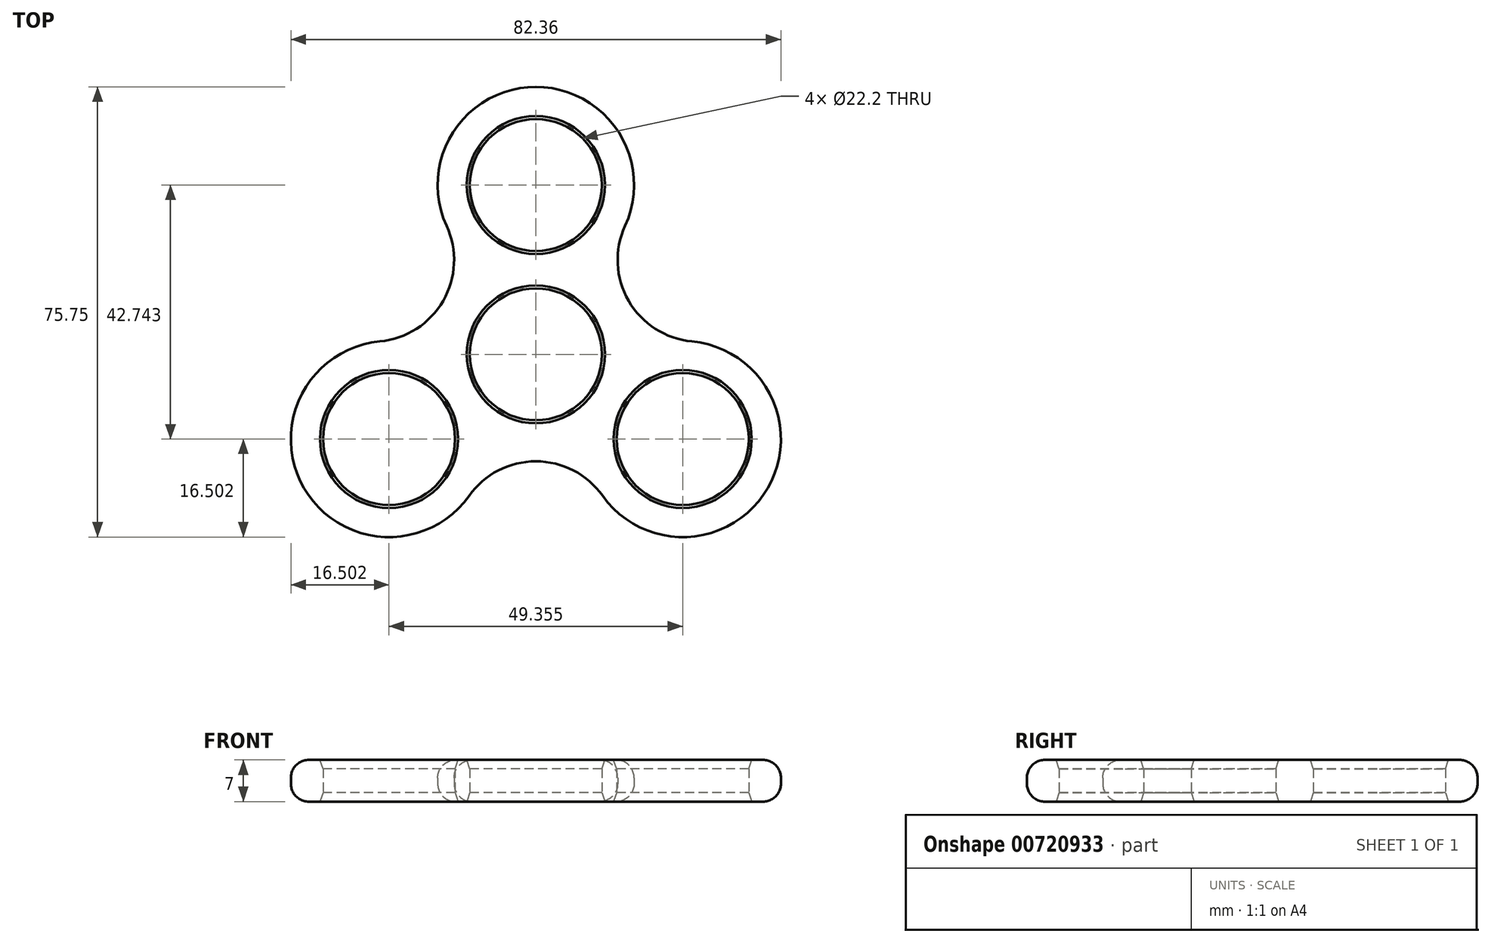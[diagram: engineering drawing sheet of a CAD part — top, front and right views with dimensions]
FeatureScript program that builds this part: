
annotation { "Feature Type Name" : "Feature", "Feature Type Description" : "" }
export const myFeature = defineFeature(function(context is Context, id is Id, definition is map)
    precondition{}
    {
        {
            var Q0;
            Q0=qCreatedBy(makeId("Top.planeOp"),FACE);
            var sketch = newSketch(context, id + "F0", { "sketchPlane" : qUnion([Q0])});
            skLineSegment(sketch, "E0", {"start": v(0, 0) * mm, "end": v(-15.59, 9) * mm, "construction": true});
            skArc(sketch, "E1", {"start": v(0, 45) * mm, "mid": v(-13.9, 37.4) * mm, "end": v(-15, 21.6) * mm});
            skArc(sketch, "E2", {"start": v(-15, 21.6) * mm, "mid": v(-13.76, 15.23) * mm, "end": v(-15.59, 9) * mm});
            skLineSegment(sketch, "E3", {"start": v(0, 0) * mm, "end": v(0, 45) * mm, "construction": true});
            skArc(sketch, "E4.MirrorCS", {"start": v(15, 21.6) * mm, "mid": v(13.76, 15.23) * mm, "end": v(15.59, 9) * mm});
            skArc(sketch, "E5.MirrorCS", {"start": v(0, 45) * mm, "mid": v(13.9, 37.4) * mm, "end": v(15, 21.6) * mm});
            skArc(sketch, "E6.1.0", {"start": v(-11.21, -23.8) * mm, "mid": v(-6.31, -19.53) * mm, "end": v(0, -18) * mm});
            skArc(sketch, "E6.1.1", {"start": v(-38.97, -22.5) * mm, "mid": v(-25.45, -30.73) * mm, "end": v(-11.21, -23.8) * mm});
            skArc(sketch, "E6.1.2", {"start": v(-38.97, -22.5) * mm, "mid": v(-39.34, -6.67) * mm, "end": v(-26.21, 2.19) * mm});
            skArc(sketch, "E6.1.3", {"start": v(-26.21, 2.19) * mm, "mid": v(-20.07, 4.3) * mm, "end": v(-15.59, 9) * mm});
            skArc(sketch, "E6.2.0", {"start": v(26.21, 2.19) * mm, "mid": v(20.07, 4.3) * mm, "end": v(15.59, 9) * mm});
            skArc(sketch, "E6.2.1", {"start": v(38.97, -22.5) * mm, "mid": v(39.34, -6.67) * mm, "end": v(26.21, 2.19) * mm});
            skArc(sketch, "E6.2.2", {"start": v(38.97, -22.5) * mm, "mid": v(25.45, -30.73) * mm, "end": v(11.21, -23.8) * mm});
            skArc(sketch, "E6.2.3", {"start": v(11.21, -23.8) * mm, "mid": v(6.31, -19.53) * mm, "end": v(0, -18) * mm});
            skPoint(sketch, "E6.center", {"position": v(0, 0) * mm});
            skCircle(sketch, "E7", {"center": v(0, 0) * mm, "radius": 11.1 * mm});
            skCircle(sketch, "E8", {"center": v(0, 28.5) * mm, "radius": 11.1 * mm});
            skCircle(sketch, "E9.1.1", {"center": v(-24.68, -14.25) * mm, "radius": 11.1 * mm});
            skCircle(sketch, "E9.2.1", {"center": v(24.68, -14.25) * mm, "radius": 11.1 * mm});
            skSolve(sketch);
        }
        {
            var Q0;
            Q0=makeQuery(id+"F0.imprint","IMPRINT",FACE,{"disambiguationData":[TD([[makeQuery(id+"F0.imprint","IMPRINT",EDGE,{"derivedFrom":sQuery(id+"F0.wireOp",EDGE,"E1")}),1.0]])]});
            extrude(context, id + "F1", {"entities" : qUnion([Q0]), "depth" : 7 * mm});
        }
        {
            var Q0;
            Q0=makeQuery(id+"F1.opExtrude","CAP_EDGE",EDGE,{"disambiguationData":[OSD([sQuery(id+"F0.wireOp",EDGE,"E6.1.1"),sQuery(id+"F0.wireOp",EDGE,"E6.1.2")])],"isStart":false});
            var Q1;
            Q1=makeQuery(id+"F1.opExtrude","CAP_EDGE",EDGE,{"disambiguationData":[OSD([sQuery(id+"F0.wireOp",EDGE,"E6.1.0"),sQuery(id+"F0.wireOp",EDGE,"E6.2.3")])],"isStart":false});
            var Q2;
            Q2=makeQuery(id+"F1.opExtrude","CAP_EDGE",EDGE,{"disambiguationData":[OSD([sQuery(id+"F0.wireOp",EDGE,"E6.2.1"),sQuery(id+"F0.wireOp",EDGE,"E6.2.2")])],"isStart":false});
            var Q3;
            Q3=makeQuery(id+"F1.opExtrude","CAP_EDGE",EDGE,{"disambiguationData":[OSD([sQuery(id+"F0.wireOp",EDGE,"E4.MirrorCS"),sQuery(id+"F0.wireOp",EDGE,"E6.2.0")])],"isStart":false});
            var Q4;
            Q4=makeQuery(id+"F1.opExtrude","CAP_EDGE",EDGE,{"disambiguationData":[OSD([sQuery(id+"F0.wireOp",EDGE,"E6.1.1"),sQuery(id+"F0.wireOp",EDGE,"E6.1.2")])],"isStart":true});
            fillet(context, id + "F2", {"entities" : qUnion([Q0, Q1, Q2, Q3, Q4]), "radius" : 3 * mm, "tangentPropagation" : true, "allowEdgeOverflow" : false});
        }
        {
            var Q0;
            Q0=makeQuery(id+"F1.opExtrude","CAP_EDGE",EDGE,{"disambiguationData":[OSD([sQuery(id+"F0.wireOp",EDGE,"E8")])],"isStart":false});
            var Q1;
            Q1=makeQuery(id+"F1.opExtrude","CAP_EDGE",EDGE,{"disambiguationData":[OSD([sQuery(id+"F0.wireOp",EDGE,"E9.1.1")])],"isStart":false});
            var Q2;
            Q2=makeQuery(id+"F1.opExtrude","CAP_EDGE",EDGE,{"disambiguationData":[OSD([sQuery(id+"F0.wireOp",EDGE,"E8")])],"isStart":true});
            var Q3;
            Q3=makeQuery(id+"F1.opExtrude","CAP_EDGE",EDGE,{"disambiguationData":[OSD([sQuery(id+"F0.wireOp",EDGE,"E9.2.1")])],"isStart":false});
            var Q4;
            Q4=makeQuery(id+"F1.opExtrude","CAP_EDGE",EDGE,{"disambiguationData":[OSD([sQuery(id+"F0.wireOp",EDGE,"E7")])],"isStart":false});
            chamfer(context, id + "F3", {"entities" : qUnion([Q0, Q1, Q2, Q3, Q4]), "chamferType" : ChamferType.TWO_OFFSETS, "width1" : 1.5 * mm, "oppositeDirection" : false, "width2" : .5 * mm, "tangentPropagation" : true});
        }
        {
            var Q0;
            Q0=makeQuery(id+"F1.opExtrude","CAP_EDGE",EDGE,{"disambiguationData":[OSD([sQuery(id+"F0.wireOp",EDGE,"E9.1.1")])],"isStart":true});
            var Q1;
            Q1=makeQuery(id+"F1.opExtrude","CAP_EDGE",EDGE,{"disambiguationData":[OSD([sQuery(id+"F0.wireOp",EDGE,"E7")])],"isStart":true});
            var Q2;
            Q2=makeQuery(id+"F1.opExtrude","CAP_EDGE",EDGE,{"disambiguationData":[OSD([sQuery(id+"F0.wireOp",EDGE,"E9.2.1")])],"isStart":true});
            chamfer(context, id + "F4", {"entities" : qUnion([Q0, Q1, Q2]), "chamferType" : ChamferType.TWO_OFFSETS, "width1" : .5 * mm, "oppositeDirection" : false, "width2" : 1.5 * mm, "tangentPropagation" : true});
        }
    });
